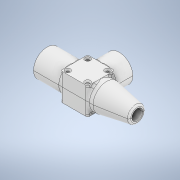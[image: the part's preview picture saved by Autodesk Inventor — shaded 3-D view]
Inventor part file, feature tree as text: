
AUTODESK INVENTOR PART (.ipt)
format: ipt  version: 2020 (Build 240168000, 168)  size: 858,624 bytes
history: native  units: mm
features: sketch x9, extrude x8, fillet x5, move_body x3, plane x2, chamfer x2, direct_edit x1, hole x1, split x1, projected_geometry x1
ambient origin geometry x8: Origin, YZ Plane, XZ Plane, XY Plane, X Axis, Y Axis, Z Axis, Center Point
bodies: Solid1 (feature_tree), Solid2 (feature_tree), Solid3 (feature_tree)
feature tree (33):
  extrude  "Extrusion1"  Depth=30.0mm
  extrude  "Extrusion2"  Depth=30.0mm
  extrude  "Extrusion3"  Depth=40.0mm TaperAngle=0.0deg
  extrude  "Extrusion4"  Depth=30.0mm TaperAngle=0.0deg
  direct_edit  "Direct Edit1"
  plane  "Work Plane1"
  extrude  "Extrusion6"  Depth=30.0mm
  fillet  "Fillet1"  Radius=20.0mm
  fillet  "Fillet2"  [1 undecoded]
  plane  "Work Plane2"
  extrude  "Extrusion7"  Depth=12.75mm
  fillet  "Fillet3"  Radius=12.8mm
  extrude  "Extrusion8"  Depth=4.0mm
  hole  "Hole1"  [1 undecoded]
  extrude  "Extrusion9"  [1 undecoded]
  fillet  "Fillet4"  Radius=20.4mm
  chamfer  "Chamfer1"  Distance=1.0mm
  fillet  "Fillet5"  Radius=0.5mm
  chamfer  "Chamfer2"  Distance=12.1mm
  split  "Split1"
  sketch  "Sketch1"  dims[d0=30.0mm d1=30.0mm]
  sketch  "Sketch2"  dims[d2=30.0mm d3=0.0mm d4=30.0mm]
  projected_geometry  "Projected Loop1"
  sketch  "Sketch3"  dims[d5=8.0mm d6=40.0mm d7=0.0mm]
  sketch  "Sketch4"  dims[d8=30.0mm d9=30.0mm d10=0.0mm]
  sketch  "Sketch6"  dims[d11=8.0mm d12=30.0mm d13=20.0mm d14=0.0mm]
  sketch  "Sketch7"  dims[d19=0.0mm d20=0.0mm d21=-14.5mm]
  sketch  "Sketch8"  dims[d22=0.0mm d23=0.0mm d24=-27.0mm]
  sketch  "Sketch9"  dims[d25=0.0mm d26=0.0mm d27=-15.0mm d28=-15.0mm]
  sketch  "Sketch10"  dims[d29=12.75mm d30=12.75mm d31=12.8mm d32=0.0mm d33=4.0mm d34=0.5mm d35=-30.0mm d36=20.4mm d37=1.0mm d38=0.0mm d39=0.5mm d40=12.1mm d41=25.0mm d42=0.0mm d43=22.0mm d44=22.0mm d45=3.0mm d46=6.0mm d47=6.0mm d48=2.0mm d49=90.0deg d50=8.0mm d51=20.594885mm d52=6.0mm d53=4.0mm d54=0.0mm d55=2.0mm d56=6.0mm d57=2.0mm d58=13.962634mm d59=2.0mm d60=6.0mm d61=2.0mm d62=13.962634mm]
  move_body  "Move1"
  move_body  "Move2"
  move_body  "Move3"
note: 3 required parameter values undecoded (feature->parameter linkage not recoverable at this tier; creation-order binding heuristic only, values carry confidence <= 0.55)
